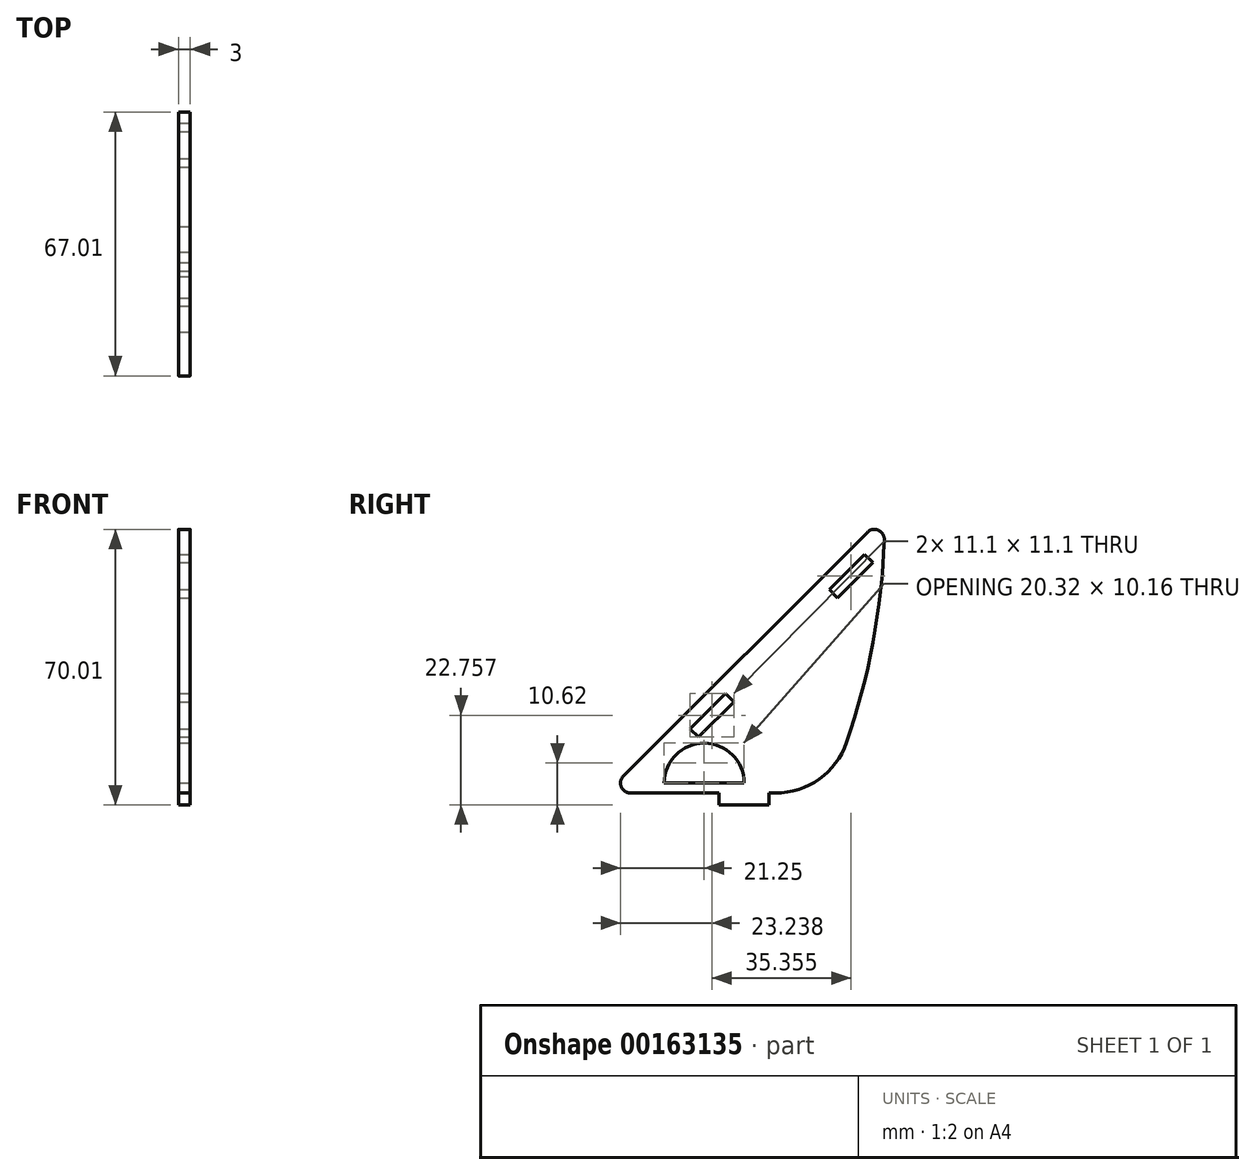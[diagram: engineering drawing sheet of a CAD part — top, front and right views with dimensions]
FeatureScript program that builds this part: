
annotation { "Feature Type Name" : "Feature", "Feature Type Description" : "" }
export const myFeature = defineFeature(function(context is Context, id is Id, definition is map)
    precondition{}
    {
        {
            var Q0;
            Q0=qCreatedBy(makeId("Right.planeOp"),FACE);
            var sketch = newSketch(context, id + "F0", { "sketchPlane" : qUnion([Q0])});
            skLineSegment(sketch, "E0", {"start": v(0, 0) * mm, "end": v(70.71, 70.71) * mm});
            skLineSegment(sketch, "E1", {"start": v(70.71, 70.71) * mm, "end": v(70.71, 0) * mm, "construction": true});
            skLineSegment(sketch, "E2", {"start": v(56.03, 0) * mm, "end": v(41.35, 0) * mm});
            skLineSegment(sketch, "E3", {"start": v(28.65, 0) * mm, "end": v(28.65, -3) * mm});
            skLineSegment(sketch, "E4", {"start": v(28.65, -3) * mm, "end": v(41.35, -3) * mm});
            skLineSegment(sketch, "E5", {"start": v(41.35, -3) * mm, "end": v(41.35, 0) * mm});
            skLineSegment(sketch, "E6", {"start": v(35, -3) * mm, "end": v(35, 0) * mm, "construction": true});
            skLineSegment(sketch, "E7.trimOffspring", {"start": v(28.65, 0) * mm, "end": v(0, 0) * mm});
            skPoint(sketch, "E8.orphan", {"position": v(70.71, 0) * mm});
            skArc(sketch, "E9", {"start": v(56.03, 0) * mm, "mid": v(67, 34.6) * mm, "end": v(70.71, 70.71) * mm});
            skSolve(sketch);
        }
        {
            var Q0;
            Q0 = qSketchRegion(id + "F0", true);
            extrude(context, id + "F1", {"entities" : qUnion([Q0]), "depth" : 3 * mm});
        }
        {
            var Q0;
            Q0=makeQuery(id+"F1.opExtrude","SWEPT_EDGE",EDGE,{"disambiguationData":[OSD([sQuery(id+"F0.wireOp",EDGE,"E2"),sQuery(id+"F0.wireOp",EDGE,"E9")])]});
            fillet(context, id + "F2", {"entities" : qUnion([Q0]), "radius" : 19.05 * mm, "tangentPropagation" : true, "allowEdgeOverflow" : false});
        }
        {
            var Q0;
            Q0=makeQuery(id+"F1.opExtrude","SWEPT_EDGE",EDGE,{"disambiguationData":[OSD([sQuery(id+"F0.wireOp",EDGE,"E0"),sQuery(id+"F0.wireOp",EDGE,"E9")])]});
            var Q1;
            Q1=makeQuery(id+"F1.opExtrude","SWEPT_EDGE",EDGE,{"disambiguationData":[OSD([sQuery(id+"F0.wireOp",EDGE,"E0"),sQuery(id+"F0.wireOp",EDGE,"E7.trimOffspring")])]});
            fillet(context, id + "F3", {"entities" : qUnion([Q0, Q1]), "radius" : 2.54 * mm, "tangentPropagation" : true, "allowEdgeOverflow" : false});
        }
        {
            var Q0;
            Q0=makeQuery(id+"F1.opExtrude","CAP_FACE",FACE,{"disambiguationData":[OSD([sQuery(id+"F0.wireOp",EDGE,"E0"),sQuery(id+"F0.wireOp",EDGE,"E2"),sQuery(id+"F0.wireOp",EDGE,"E3"),sQuery(id+"F0.wireOp",EDGE,"E4"),sQuery(id+"F0.wireOp",EDGE,"E5"),sQuery(id+"F0.wireOp",EDGE,"E7.trimOffspring"),sQuery(id+"F0.wireOp",EDGE,"E9")])],"isStart":false});
            var sketch = newSketch(context, id + "F4", { "sketchPlane" : qUnion([Q0])});
            skLineSegment(sketch, "E10.0", {"start": v(7.07, 0) * mm, "end": v(69.4, 62.32) * mm, "construction": true});
            skLineSegment(sketch, "E11", {"start": v(21.28, 16.33) * mm, "end": v(23.4, 14.2) * mm});
            skLineSegment(sketch, "E12", {"start": v(23.4, 14.2) * mm, "end": v(32.38, 23.19) * mm});
            skLineSegment(sketch, "E13", {"start": v(32.38, 23.19) * mm, "end": v(30.26, 25.3) * mm});
            skLineSegment(sketch, "E14", {"start": v(30.26, 25.3) * mm, "end": v(21.28, 16.33) * mm});
            skLineSegment(sketch, "E15", {"start": v(25.77, 20.82) * mm, "end": v(27.89, 18.7) * mm, "construction": true});
            skPoint(sketch, "E16", {"position": v(26.83, 19.76) * mm});
            skLineSegment(sketch, "E17", {"start": v(56.63, 51.68) * mm, "end": v(58.75, 49.56) * mm});
            skLineSegment(sketch, "E18", {"start": v(58.75, 49.56) * mm, "end": v(67.73, 58.54) * mm});
            skLineSegment(sketch, "E19", {"start": v(67.73, 58.54) * mm, "end": v(65.61, 60.66) * mm});
            skLineSegment(sketch, "E20", {"start": v(65.61, 60.66) * mm, "end": v(56.63, 51.68) * mm});
            skLineSegment(sketch, "E21", {"start": v(61.12, 56.17) * mm, "end": v(63.24, 54.05) * mm, "construction": true});
            skPoint(sketch, "E22", {"position": v(62.18, 55.11) * mm});
            skSolve(sketch);
        }
        {
            var Q0;
            Q0 = qSketchRegion(id + "F4", true);
            extrude(context, id + "F5", {"entities" : qUnion([Q0]), "operationType" : NewBodyOperationType.REMOVE, "endBound" : BoundingType.UP_TO_NEXT, "oppositeDirection" : true, "depth" : 25.4 * mm});
        }
        {
            var Q0;
            Q0=makeQuery(id+"F1.opExtrude","CAP_FACE",FACE,{"disambiguationData":[OSD([sQuery(id+"F0.wireOp",EDGE,"E0"),sQuery(id+"F0.wireOp",EDGE,"E2"),sQuery(id+"F0.wireOp",EDGE,"E3"),sQuery(id+"F0.wireOp",EDGE,"E4"),sQuery(id+"F0.wireOp",EDGE,"E5"),sQuery(id+"F0.wireOp",EDGE,"E7.trimOffspring"),sQuery(id+"F0.wireOp",EDGE,"E9")])],"isStart":false});
            var sketch = newSketch(context, id + "F6", { "sketchPlane" : qUnion([Q0])});
            skArc(sketch, "E23", {"start": v(35, 2.54) * mm, "mid": v(24.84, 12.7) * mm, "end": v(14.68, 2.54) * mm});
            skPoint(sketch, "E23.startSnap0", {"position": v(35, -3) * mm});
            skLineSegment(sketch, "E24", {"start": v(14.68, 2.54) * mm, "end": v(35, 2.54) * mm});
            skSolve(sketch);
        }
        {
            var Q0;
            Q0 = qSketchRegion(id + "F6", true);
            extrude(context, id + "F7", {"entities" : qUnion([Q0]), "operationType" : NewBodyOperationType.REMOVE, "endBound" : BoundingType.UP_TO_NEXT, "oppositeDirection" : true, "depth" : 25.4 * mm});
        }
    });
